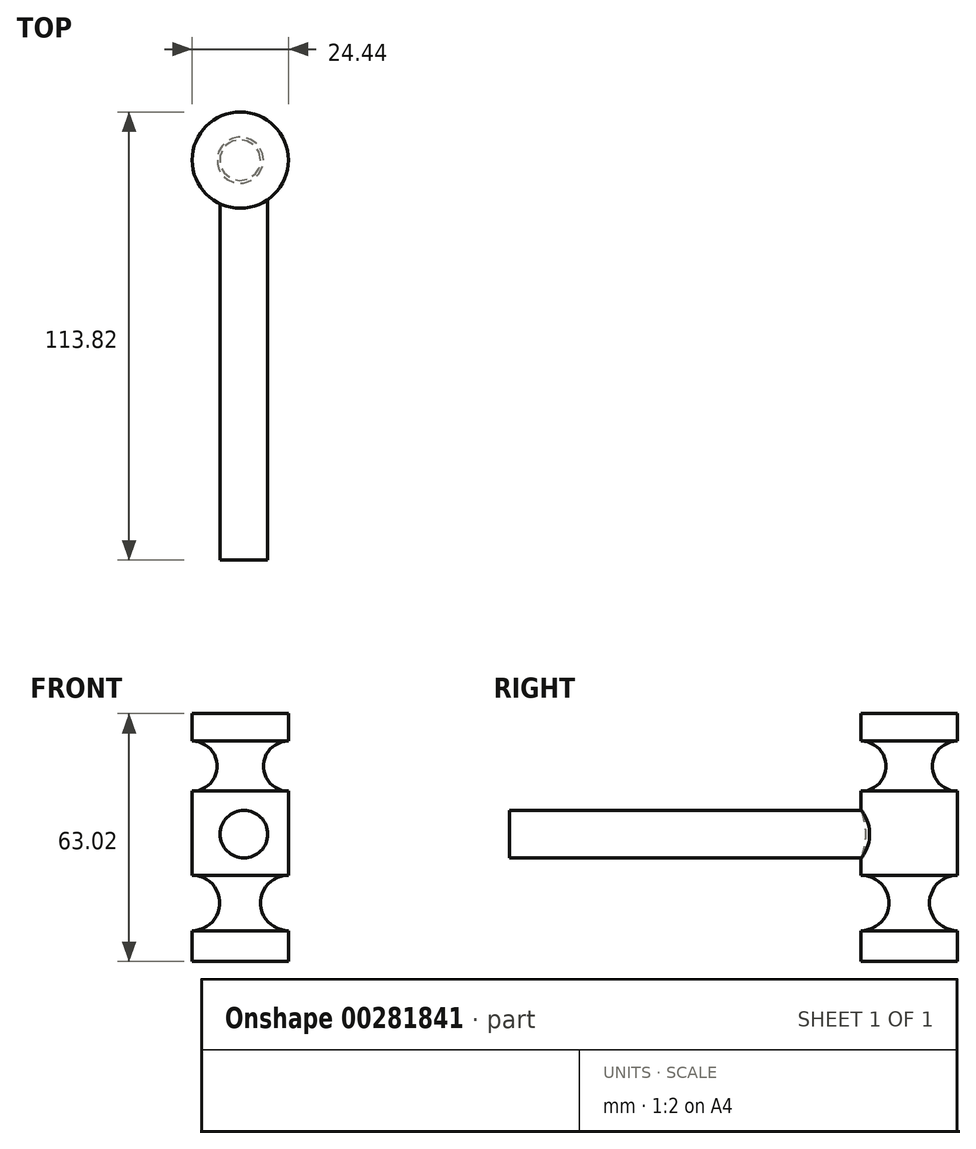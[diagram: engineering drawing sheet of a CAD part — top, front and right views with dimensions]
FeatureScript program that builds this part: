
annotation { "Feature Type Name" : "Feature", "Feature Type Description" : "" }
export const myFeature = defineFeature(function(context is Context, id is Id, definition is map)
    precondition{}
    {
        {
            var Q0;
            Q0=qCreatedBy(makeId("Front.planeOp"),FACE);
            var sketch = newSketch(context, id + "F0", { "sketchPlane" : qUnion([Q0])});
            skLineSegment(sketch, "E0", {"start": v(0, 0) * mm, "end": v(0, 7.85) * mm});
            skLineSegment(sketch, "E1", {"start": v(0, 63.02) * mm, "end": v(-12.22, 63.02) * mm});
            skLineSegment(sketch, "E2", {"start": v(-12.22, 63.02) * mm, "end": v(-12.22, 0) * mm});
            skLineSegment(sketch, "E3", {"start": v(-12.22, 0) * mm, "end": v(0, 0) * mm});
            skArc(sketch, "E4", {"start": v(0, 56) * mm, "mid": v(-6.35, 49.65) * mm, "end": v(0, 43.3) * mm});
            skArc(sketch, "E5", {"start": v(0, 21.94) * mm, "mid": v(-7.04, 14.9) * mm, "end": v(0, 7.85) * mm});
            skLineSegment(sketch, "E6.trimOffspring", {"start": v(0, 56) * mm, "end": v(0, 63.02) * mm});
            skLineSegment(sketch, "E7.trimOffspring", {"start": v(0, 21.94) * mm, "end": v(0, 43.3) * mm});
            skSolve(sketch);
        }
        {
            var Q0;
            Q0=makeQuery(id+"F0.imprint","IMPRINT",FACE,{"disambiguationData":[TD([[makeQuery(id+"F0.imprint","IMPRINT",EDGE,{"derivedFrom":sQuery(id+"F0.wireOp",EDGE,"E0")}),1.0]])]});
            var Q1;
            Q1=sQuery(id+"F0.wireOp",EDGE,"E2");
            revolve(context, id + "F1", {"entities" : qUnion([Q0]), "axis" : qUnion([Q1]), "revolveType" : RevolveType.FULL});
        }
        {
            var Q0;
            Q0=qCreatedBy(makeId("Front.planeOp"),FACE);
            var sketch = newSketch(context, id + "F2", { "sketchPlane" : qUnion([Q0])});
            skCircle(sketch, "E8", {"center": v(-11.28, 32.36) * mm, "radius": 6.04 * mm});
            skSolve(sketch);
        }
        {
            var Q0;
            Q0 = qSketchRegion(id + "F2", true);
            extrude(context, id + "F3", {"entities" : qUnion([Q0]), "operationType" : NewBodyOperationType.ADD, "depth" : 101.6 * mm});
        }
    });
